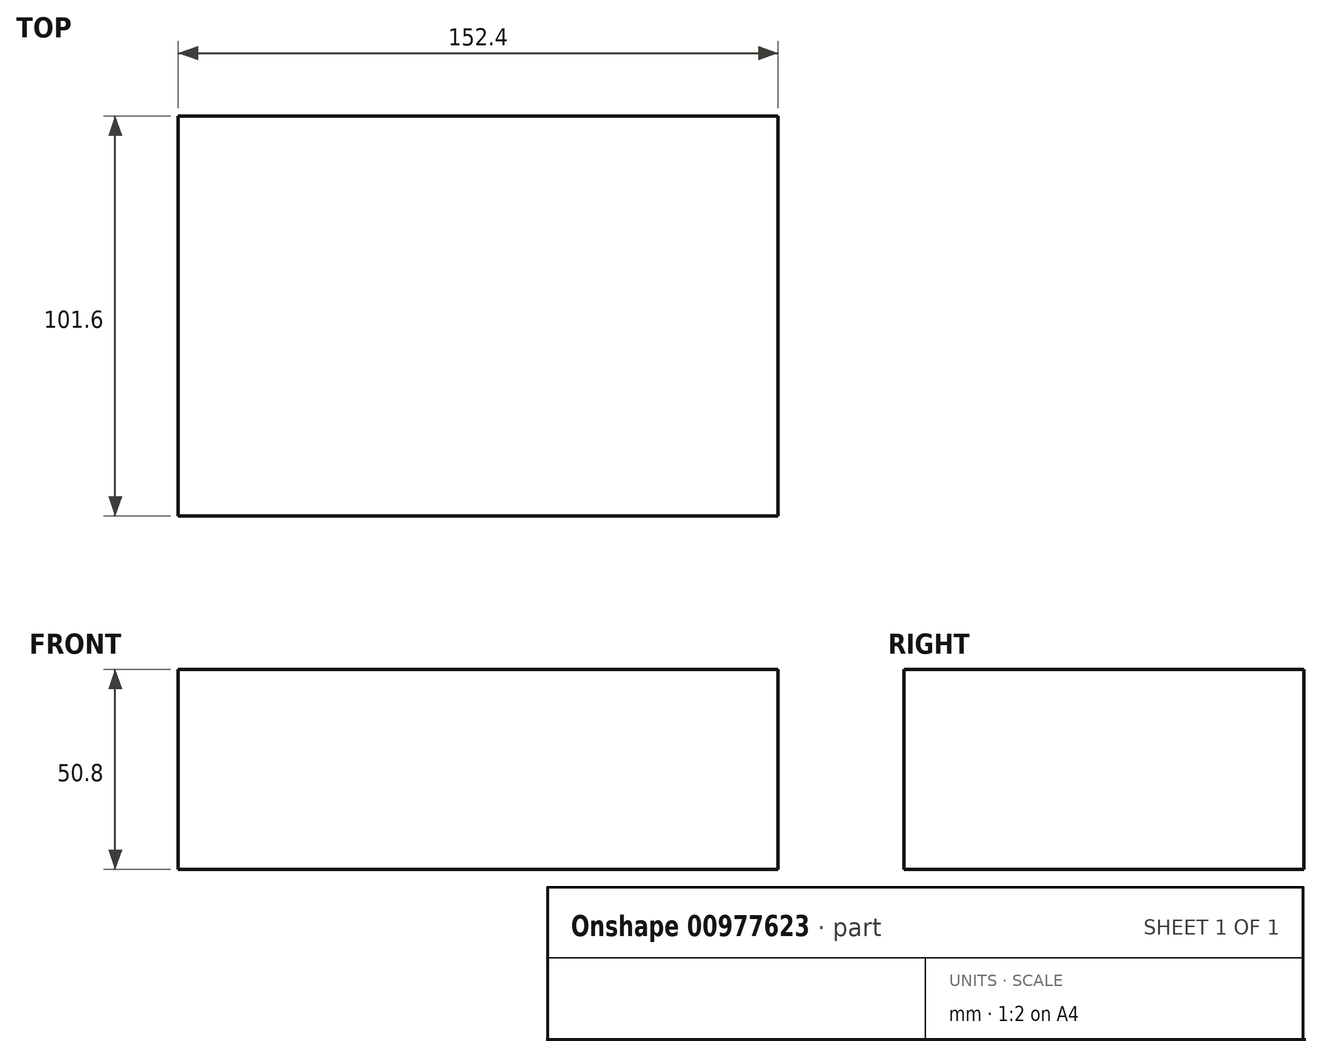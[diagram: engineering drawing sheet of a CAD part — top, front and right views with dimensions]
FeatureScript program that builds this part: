
annotation { "Feature Type Name" : "Feature", "Feature Type Description" : "" }
export const myFeature = defineFeature(function(context is Context, id is Id, definition is map)
    precondition{}
    {
        {
            var Q0;
            Q0=qCreatedBy(makeId("Top.planeOp"),FACE);
            var sketch = newSketch(context, id + "F0", { "sketchPlane" : qUnion([Q0])});
            skLineSegment(sketch, "E0.bottom", {"start": v(-76.2, 50.8) * mm, "end": v(76.2, 50.8) * mm});
            skLineSegment(sketch, "E0.top", {"start": v(-76.2, -50.8) * mm, "end": v(76.2, -50.8) * mm});
            skLineSegment(sketch, "E0.left", {"start": v(-76.2, 50.8) * mm, "end": v(-76.2, -50.8) * mm});
            skLineSegment(sketch, "E0.right", {"start": v(76.2, 50.8) * mm, "end": v(76.2, -50.8) * mm});
            skPoint(sketch, "E0.middle", {"position": v(0, 0) * mm});
            skSolve(sketch);
        }
        {
            var Q0;
            Q0=makeQuery(id+"F0.imprint","IMPRINT",FACE,{"disambiguationData":[TD([[makeQuery(id+"F0.imprint","IMPRINT",EDGE,{"derivedFrom":sQuery(id+"F0.wireOp",EDGE,"E0.bottom")}),-1.0]])]});
            extrude(context, id + "F1", {"entities" : qUnion([Q0]), "depth" : 50.8 * mm, "offsetDistance" : 25 * mm});
        }
    });
